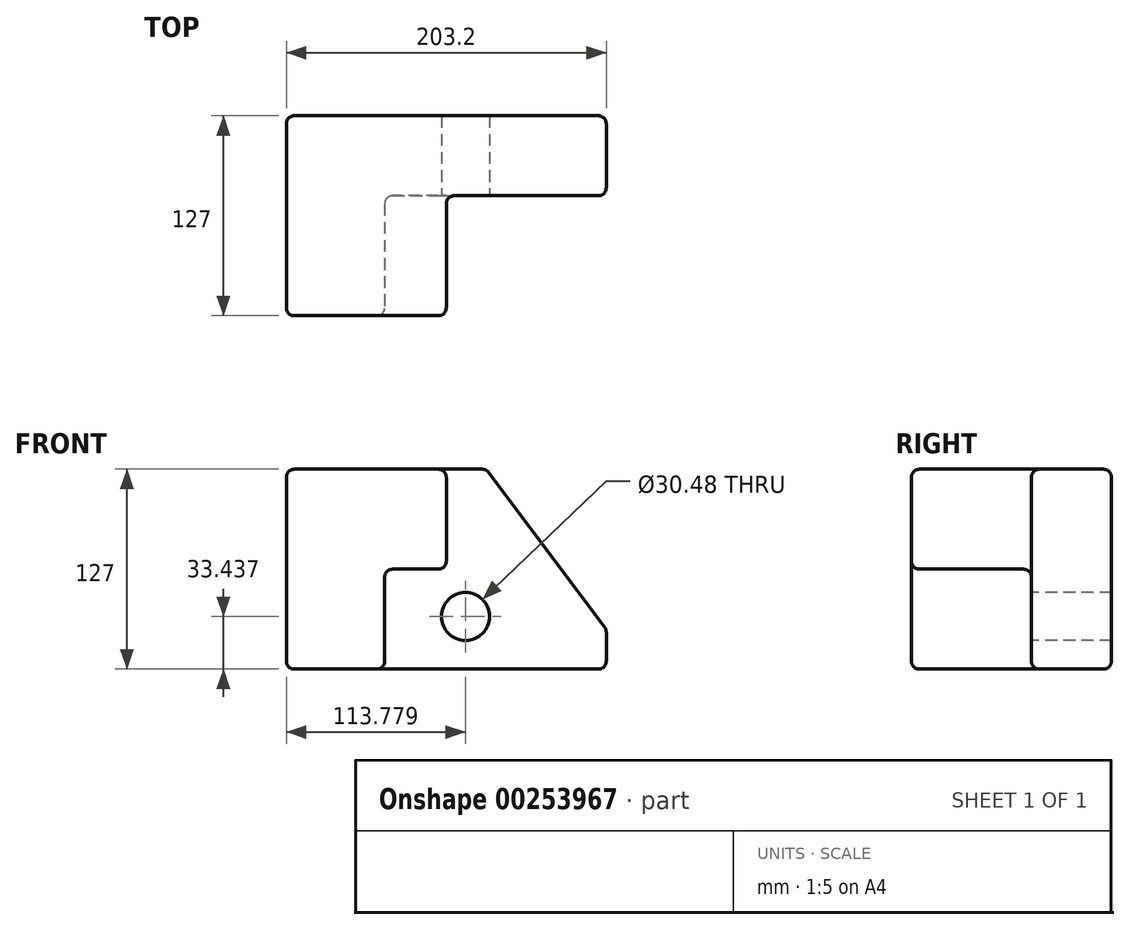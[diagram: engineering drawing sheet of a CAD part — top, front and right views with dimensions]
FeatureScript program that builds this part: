
annotation { "Feature Type Name" : "Feature", "Feature Type Description" : "" }
export const myFeature = defineFeature(function(context is Context, id is Id, definition is map)
    precondition{}
    {
        {
            var Q0;
            Q0=qCreatedBy(makeId("Front.planeOp"),FACE);
            var sketch = newSketch(context, id + "F0", { "sketchPlane" : qUnion([Q0])});
            skLineSegment(sketch, "E0.bottom", {"start": v(-101.6, 63.5) * mm, "end": v(101.6, 63.5) * mm});
            skLineSegment(sketch, "E0.top", {"start": v(-101.6, -63.5) * mm, "end": v(101.6, -63.5) * mm});
            skLineSegment(sketch, "E0.left", {"start": v(-101.6, 63.5) * mm, "end": v(-101.6, -63.5) * mm});
            skLineSegment(sketch, "E0.right", {"start": v(101.6, 63.5) * mm, "end": v(101.6, -63.5) * mm});
            skPoint(sketch, "E0.middle", {"position": v(0, 0) * mm});
            skSolve(sketch);
        }
        {
            var Q0;
            Q0=makeQuery(id+"F0.imprint","IMPRINT",FACE,{"disambiguationData":[TD([[makeQuery(id+"F0.imprint","IMPRINT",EDGE,{"derivedFrom":sQuery(id+"F0.wireOp",EDGE,"E0.bottom")}),-1.0]])]});
            extrude(context, id + "F1", {"entities" : qUnion([Q0]), "depth" : 127 * mm});
        }
        {
            var Q0;
            Q0=makeQuery(id+"F1.opExtrude","CAP_FACE",FACE,{"disambiguationData":[OSD([sQuery(id+"F0.wireOp",EDGE,"E0.bottom"),sQuery(id+"F0.wireOp",EDGE,"E0.top"),sQuery(id+"F0.wireOp",EDGE,"E0.left"),sQuery(id+"F0.wireOp",EDGE,"E0.right")])],"isStart":false});
            var sketch = newSketch(context, id + "F2", { "sketchPlane" : qUnion([Q0])});
            skLineSegment(sketch, "E1", {"start": v(-101.6, 63.5) * mm, "end": v(0, 63.5) * mm});
            skLineSegment(sketch, "E2", {"start": v(0, 63.5) * mm, "end": v(0, 0) * mm});
            skLineSegment(sketch, "E3", {"start": v(0, 0) * mm, "end": v(-39.13, 0) * mm});
            skLineSegment(sketch, "E4", {"start": v(-39.13, 0) * mm, "end": v(-39.13, -63.5) * mm});
            skLineSegment(sketch, "E5", {"start": v(-39.13, -63.5) * mm, "end": v(-101.6, -63.5) * mm});
            skLineSegment(sketch, "E6", {"start": v(-101.6, -63.5) * mm, "end": v(-101.6, 63.5) * mm});
            skSolve(sketch);
        }
        {
            var Q0;
            {var subQ2=sQuery(id+"F2.wireOp",EDGE,"E2");Q0=makeQuery(id+"F2.imprint","IMPRINT",FACE,{"disambiguationData":[TD([[makeQuery(id+"F2.imprint","IMPRINT",EDGE,{"derivedFrom":subQ2}),1.0]])]});}
            extrude(context, id + "F3", {"entities" : qUnion([Q0]), "operationType" : NewBodyOperationType.REMOVE, "oppositeDirection" : true, "depth" : 76.2 * mm});
        }
        {
            var Q0;
            Q0=makeQuery(id+"F1.opExtrude","SWEPT_EDGE",EDGE,{"disambiguationData":[OSD([sQuery(id+"F0.wireOp",EDGE,"E0.bottom"),sQuery(id+"F0.wireOp",EDGE,"E0.right")])]});
            chamfer(context, id + "F4", {"entities" : qUnion([Q0]), "chamferType" : ChamferType.TWO_OFFSETS, "width1" : 76.2 * mm, "oppositeDirection" : false, "width2" : 101.6 * mm, "tangentPropagation" : true});
        }
        {
            var Q0;
            Q0=makeQuery(id+"F1.opExtrude","SWEPT_FACE",FACE,{"disambiguationData":[OSD([sQuery(id+"F0.wireOp",EDGE,"E0.bottom")])]});
            var Q1;
            Q1=makeQuery(id+"F1.opExtrude","CAP_FACE",FACE,{"disambiguationData":[OSD([sQuery(id+"F0.wireOp",EDGE,"E0.bottom"),sQuery(id+"F0.wireOp",EDGE,"E0.top"),sQuery(id+"F0.wireOp",EDGE,"E0.left"),sQuery(id+"F0.wireOp",EDGE,"E0.right")])],"isStart":false});
            var Q2;
            Q2=makeQuery(id+"F3.boolean.opBoolean","COPY",FACE,{"derivedFrom":makeQuery(id+"F3.opExtrude","SWEPT_FACE",FACE,{"disambiguationData":[OSD([sQuery(id+"F2.wireOp",EDGE,"E4")])]})});
            var Q3;
            Q3=makeQuery(id+"F3.boolean.opBoolean","COPY",FACE,{"derivedFrom":makeQuery(id+"F3.opExtrude","SWEPT_FACE",FACE,{"disambiguationData":[OSD([sQuery(id+"F2.wireOp",EDGE,"E2")])]})});
            var Q4;
            Q4=makeQuery(id+"F3.boolean.opBoolean","COPY",FACE,{"derivedFrom":makeQuery(id+"F3.opExtrude","CAP_FACE",FACE,{"disambiguationData":[OSD([sQuery(id+"F0.wireOp",EDGE,"E0.bottom"),sQuery(id+"F0.wireOp",EDGE,"E0.top"),sQuery(id+"F0.wireOp",EDGE,"E0.right"),sQuery(id+"F2.wireOp",EDGE,"E2"),sQuery(id+"F2.wireOp",EDGE,"E3"),sQuery(id+"F2.wireOp",EDGE,"E4")])],"isStart":false})});
            var Q5;
            Q5=makeQuery(id+"F4.opChamfer","BLEND_FACE",FACE,{"disambiguationData":[OSD([sQuery(id+"F0.wireOp",EDGE,"E0.bottom"),sQuery(id+"F0.wireOp",EDGE,"E0.right")])]});
            var Q6;
            Q6=makeQuery(id+"F1.opExtrude","SWEPT_FACE",FACE,{"disambiguationData":[OSD([sQuery(id+"F0.wireOp",EDGE,"E0.right")])]});
            var Q7;
            Q7=makeQuery(id+"F1.opExtrude","CAP_FACE",FACE,{"disambiguationData":[OSD([sQuery(id+"F0.wireOp",EDGE,"E0.bottom"),sQuery(id+"F0.wireOp",EDGE,"E0.top"),sQuery(id+"F0.wireOp",EDGE,"E0.left"),sQuery(id+"F0.wireOp",EDGE,"E0.right")])],"isStart":true});
            var Q8;
            Q8=makeQuery(id+"F1.opExtrude","SWEPT_FACE",FACE,{"disambiguationData":[OSD([sQuery(id+"F0.wireOp",EDGE,"E0.top")])]});
            var Q9;
            Q9=makeQuery(id+"F1.opExtrude","SWEPT_FACE",FACE,{"disambiguationData":[OSD([sQuery(id+"F0.wireOp",EDGE,"E0.left")])]});
            fillet(context, id + "F5", {"entities" : qUnion([Q0, Q1, Q2, Q3, Q4, Q5, Q6, Q7, Q8, Q9]), "radius" : 5.08 * mm, "tangentPropagation" : true, "allowEdgeOverflow" : false});
        }
        {
            var Q0;
            Q0=makeQuery(id+"F3.boolean.opBoolean","COPY",FACE,{"derivedFrom":makeQuery(id+"F3.opExtrude","CAP_FACE",FACE,{"disambiguationData":[OSD([sQuery(id+"F0.wireOp",EDGE,"E0.bottom"),sQuery(id+"F0.wireOp",EDGE,"E0.top"),sQuery(id+"F0.wireOp",EDGE,"E0.right"),sQuery(id+"F2.wireOp",EDGE,"E2"),sQuery(id+"F2.wireOp",EDGE,"E3"),sQuery(id+"F2.wireOp",EDGE,"E4")])],"isStart":false})});
            var sketch = newSketch(context, id + "F6", { "sketchPlane" : qUnion([Q0])});
            skCircle(sketch, "E7", {"center": v(12.18, -30.06) * mm, "radius": 15.24 * mm});
            skSolve(sketch);
        }
        {
            var Q0;
            Q0=makeQuery(id+"F6.imprint","IMPRINT",FACE,{"disambiguationData":[TD([[makeQuery(id+"F6.imprint","IMPRINT",EDGE,{"derivedFrom":sQuery(id+"F6.wireOp",EDGE,"E7")}),1.0]])]});
            extrude(context, id + "F7", {"entities" : qUnion([Q0]), "operationType" : NewBodyOperationType.REMOVE, "oppositeDirection" : true, "depth" : 76.2 * mm});
        }
    });
